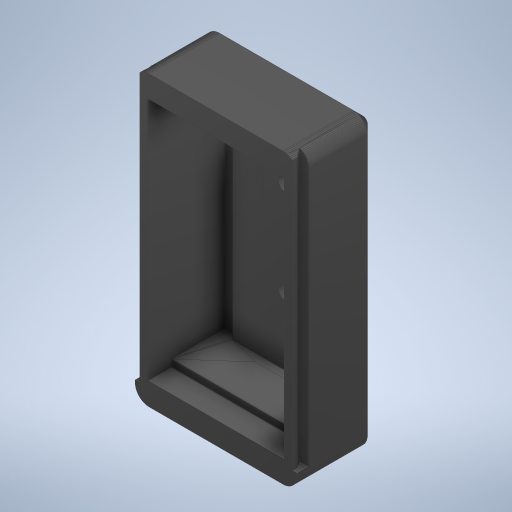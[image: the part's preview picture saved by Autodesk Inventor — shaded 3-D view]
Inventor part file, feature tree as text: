
AUTODESK INVENTOR PART (.ipt)
format: ipt  version: 2024.3 (Build 283343000, 343)  size: 1,982,464 bytes
history: native  units: mm
features: other x5, extrude x5, sketch x5
ambient origin geometry x8: Origin, YZ Plane, XZ Plane, XY Plane, X Axis, Y Axis, Z Axis, Center Point
bodies: Body1 (feature_tree), Body2 (feature_tree)
feature tree (15):
  other  "Sólido1"
  other  "ESP32_DEVKIT_V1_Case"
  other  "Coser superficie1"
  extrude  "Extrusión1"  Depth=11.479638mm
  extrude  "Extrusión2"  Depth=10.0mm TaperAngle=0.0deg
  extrude  "Extrusión3"  Depth=0.6mm
  extrude  "Extrusión4"  Depth=13.0mm
  extrude  "Extrusión5"  Depth=4.75mm
  sketch  "Boceto1"  dims[d0=11.479638mm d1=40.440399mm]
  sketch  "Boceto2"  dims[d2=9.377155mm d3=10.0mm d4=0.0mm]
  sketch  "Boceto3"  dims[d5=13.0mm d6=0.6mm]
  sketch  "Boceto4"  dims[d7=0.0mm d8=13.0mm]
  sketch  "Boceto5"  dims[d9=27.0mm d10=2.0mm d11=0.0mm d12=0.0mm d13=4.75mm d14=12.0mm d15=0.0mm d16=12.0mm d17=0.0mm d18=1.85mm d19=25.0mm d20=15.0mm d21=12.0mm d22=0.0mm d23=0.5mm d24=0.872665mm]
  other  "Compuesto1"
  other  "Sup1"
